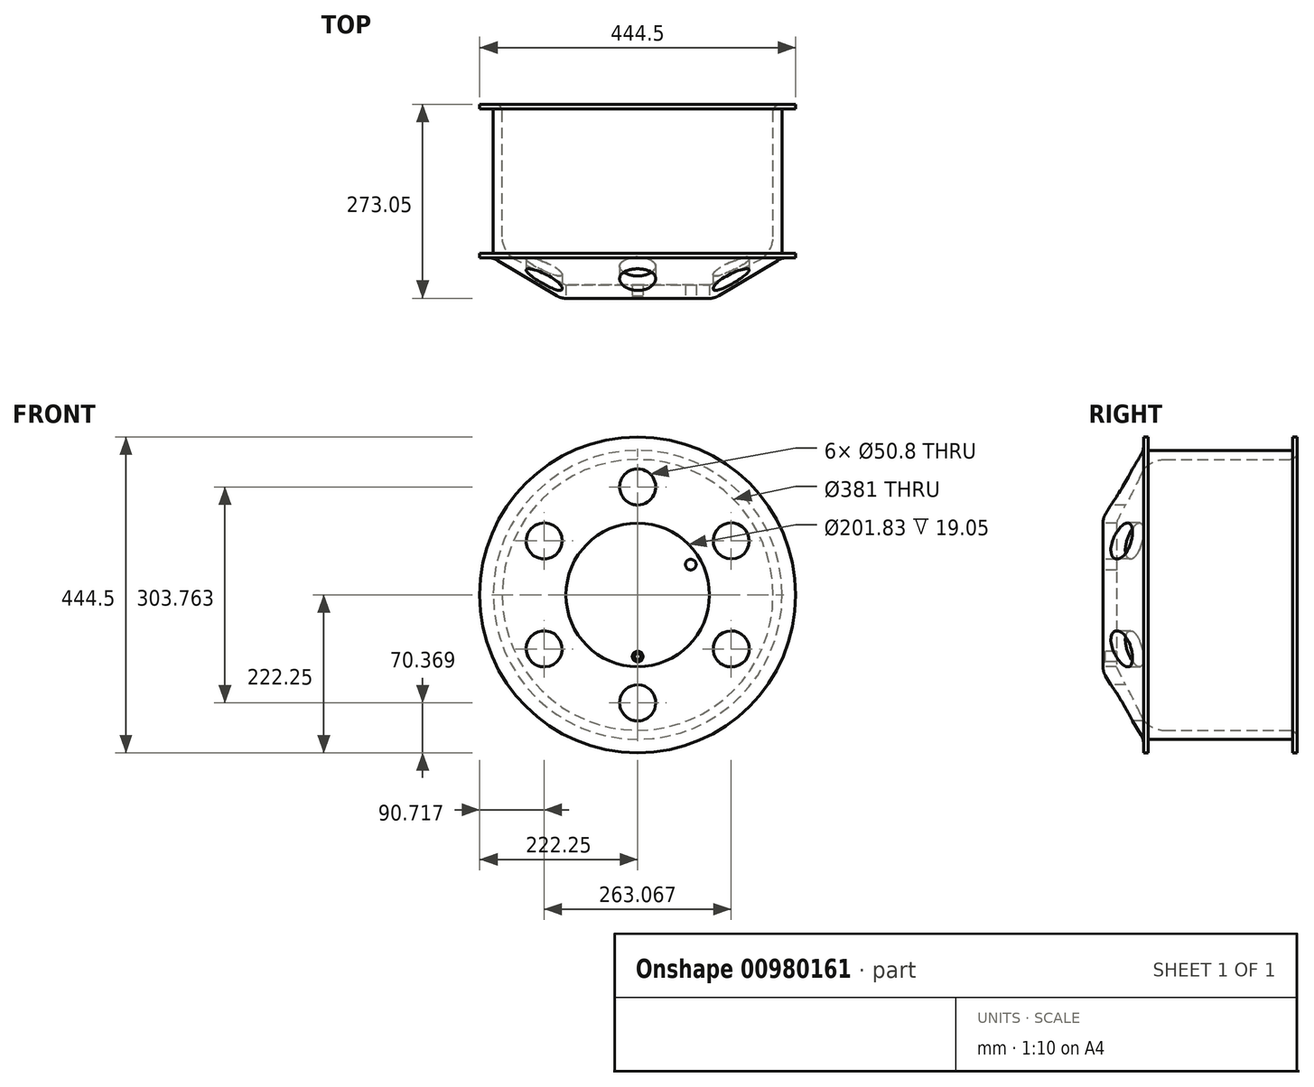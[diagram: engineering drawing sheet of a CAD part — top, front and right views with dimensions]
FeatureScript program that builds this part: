
annotation { "Feature Type Name" : "Feature", "Feature Type Description" : "" }
export const myFeature = defineFeature(function(context is Context, id is Id, definition is map)
    precondition{}
    {
        {
            var Q0;
            Q0=qCreatedBy(makeId("Right.planeOp"),FACE);
            var sketch = newSketch(context, id + "F0", { "sketchPlane" : qUnion([Q0])});
            skLineSegment(sketch, "E0", {"start": v(-78.93, 190.5) * mm, "end": v(96.9, 190.5) * mm});
            skLineSegment(sketch, "E1", {"start": v(107.07, 200.66) * mm, "end": v(107.07, 222.25) * mm});
            skLineSegment(sketch, "E2", {"start": v(107.07, 222.25) * mm, "end": v(100.72, 222.25) * mm});
            skLineSegment(sketch, "E3", {"start": v(100.72, 222.25) * mm, "end": v(100.72, 205.95) * mm});
            skLineSegment(sketch, "E4", {"start": v(97.97, 203.2) * mm, "end": v(-99.73, 203.2) * mm});
            skLineSegment(sketch, "E5", {"start": v(-102.48, 205.95) * mm, "end": v(-102.48, 222.25) * mm});
            skLineSegment(sketch, "E6", {"start": v(-102.48, 222.25) * mm, "end": v(-108.83, 222.25) * mm});
            skLineSegment(sketch, "E7", {"start": v(-108.83, 222.25) * mm, "end": v(-108.83, 210.24) * mm});
            skLineSegment(sketch, "E8", {"start": v(-112.45, 197.17) * mm, "end": v(-162.36, 113.98) * mm});
            skLineSegment(sketch, "E9", {"start": v(-165.98, 100.91) * mm, "end": v(-165.98, 0) * mm});
            skLineSegment(sketch, "E10", {"start": v(-165.98, 0) * mm, "end": v(-146.93, 0) * mm});
            skLineSegment(sketch, "E11", {"start": v(-146.93, 0) * mm, "end": v(-146.93, 101.6) * mm});
            skLineSegment(sketch, "E12", {"start": v(-146.93, 101.6) * mm, "end": v(-113.01, 169.44) * mm});
            skPoint(sketch, "E13.visualSharp", {"position": v(-102.48, 190.5) * mm});
            skArc(sketch, "E13.filletArc", {"start": v(-78.93, 190.5) * mm, "mid": v(-98.96, 184.8) * mm, "end": v(-113.01, 169.44) * mm});
            skPoint(sketch, "E14.visualSharp", {"position": v(-165.98, 107.95) * mm});
            skArc(sketch, "E14.filletArc", {"start": v(-162.36, 113.98) * mm, "mid": v(-165.06, 107.7) * mm, "end": v(-165.98, 100.91) * mm});
            skPoint(sketch, "E15.visualSharp", {"position": v(-108.83, 203.2) * mm});
            skArc(sketch, "E15.filletArc", {"start": v(-112.45, 197.17) * mm, "mid": v(-109.75, 203.46) * mm, "end": v(-108.83, 210.24) * mm});
            skPoint(sketch, "E16.visualSharp", {"position": v(-102.48, 203.2) * mm});
            skArc(sketch, "E16.filletArc", {"start": v(-102.48, 205.95) * mm, "mid": v(-101.68, 204) * mm, "end": v(-99.73, 203.2) * mm});
            skPoint(sketch, "E17.visualSharp", {"position": v(100.72, 203.2) * mm});
            skArc(sketch, "E17.filletArc", {"start": v(97.97, 203.2) * mm, "mid": v(99.92, 204) * mm, "end": v(100.72, 205.95) * mm});
            skPoint(sketch, "E18.visualSharp", {"position": v(107.07, 190.5) * mm});
            skArc(sketch, "E18.filletArc", {"start": v(96.9, 190.5) * mm, "mid": v(104.1, 193.48) * mm, "end": v(107.07, 200.66) * mm});
            skLineSegment(sketch, "E19", {"start": v(0, 0) * mm, "end": v(-85.99, 0) * mm});
            skSolve(sketch);
        }
        {
            var Q0;
            Q0=makeQuery(id+"F0.imprint","IMPRINT",FACE,{"disambiguationData":[TD([[makeQuery(id+"F0.imprint","IMPRINT",EDGE,{"derivedFrom":sQuery(id+"F0.wireOp",EDGE,"E0")}),1.0]])]});
            var Q1;
            Q1=sQuery(id+"F0.wireOp",EDGE,"E19");
            revolve(context, id + "F1", {"surfaceOperationType" : NewSurfaceOperationType.NEW, "entities" : qUnion([Q0]), "axis" : qUnion([Q1]), "revolveType" : RevolveType.FULL});
        }
        {
            var Q0;
            Q0=makeQuery(id+"F1.opRevolve","SWEPT_FACE",FACE,{"disambiguationData":[OSD([sQuery(id+"F0.wireOp",EDGE,"E9")])]});
            var sketch = newSketch(context, id + "F2", { "sketchPlane" : qUnion([Q0])});
            skCircle(sketch, "E20", {"center": v(0, 0) * mm, "radius": 85.72 * mm});
            skCircle(sketch, "E21", {"center": v(0, 85.73) * mm, "radius": 7.5 * mm});
            skCircle(sketch, "E22.1.0", {"center": v(-74.69, 42.6) * mm, "radius": 7.5 * mm});
            skCircle(sketch, "E22.2.0", {"center": v(-74.69, -43.64) * mm, "radius": 7.5 * mm});
            skCircle(sketch, "E22.3.0", {"center": v(0, -86.76) * mm, "radius": 7.5 * mm});
            skCircle(sketch, "E22.4.0", {"center": v(74.69, -43.64) * mm, "radius": 7.5 * mm});
            skCircle(sketch, "E22.5.0", {"center": v(74.69, 42.6) * mm, "radius": 7.5 * mm});
            skPoint(sketch, "E22.center", {"position": v(0, -0.52) * mm});
            skCircle(sketch, "E23", {"center": v(0, 0) * mm, "radius": 67.5 * mm});
            skCircle(sketch, "E24", {"center": v(0, 151.88) * mm, "radius": 25.4 * mm});
            skCircle(sketch, "E25.1.0", {"center": v(-131.53, 75.94) * mm, "radius": 25.4 * mm});
            skCircle(sketch, "E25.2.0", {"center": v(-131.53, -75.94) * mm, "radius": 25.4 * mm});
            skCircle(sketch, "E25.3.0", {"center": v(0, -151.88) * mm, "radius": 25.4 * mm});
            skCircle(sketch, "E25.4.0", {"center": v(131.53, -75.94) * mm, "radius": 25.4 * mm});
            skCircle(sketch, "E25.5.0", {"center": v(131.53, 75.94) * mm, "radius": 25.4 * mm});
            skSolve(sketch);
        }
        {
            var Q0;
            Q0=makeQuery(id+"F2.imprint","IMPRINT",FACE,{"disambiguationData":[TD([[makeQuery(id+"F2.imprint","IMPRINT",EDGE,{"derivedFrom":sQuery(id+"F2.wireOp",EDGE,"E24")}),1.0]])]});
            var Q1;
            Q1=makeQuery(id+"F2.imprint","IMPRINT",FACE,{"disambiguationData":[TD([[makeQuery(id+"F2.imprint","IMPRINT",EDGE,{"derivedFrom":sQuery(id+"F2.wireOp",EDGE,"E25.1.0")}),1.0]])]});
            var Q2;
            Q2=makeQuery(id+"F2.imprint","IMPRINT",FACE,{"disambiguationData":[TD([[makeQuery(id+"F2.imprint","IMPRINT",EDGE,{"derivedFrom":sQuery(id+"F2.wireOp",EDGE,"E25.2.0")}),1.0]])]});
            var Q3;
            Q3=makeQuery(id+"F2.imprint","IMPRINT",FACE,{"disambiguationData":[TD([[makeQuery(id+"F2.imprint","IMPRINT",EDGE,{"derivedFrom":sQuery(id+"F2.wireOp",EDGE,"E25.3.0")}),1.0]])]});
            var Q4;
            Q4=makeQuery(id+"F2.imprint","IMPRINT",FACE,{"disambiguationData":[TD([[makeQuery(id+"F2.imprint","IMPRINT",EDGE,{"derivedFrom":sQuery(id+"F2.wireOp",EDGE,"E25.4.0")}),1.0]])]});
            var Q5;
            Q5=makeQuery(id+"F2.imprint","IMPRINT",FACE,{"disambiguationData":[TD([[makeQuery(id+"F2.imprint","IMPRINT",EDGE,{"derivedFrom":sQuery(id+"F2.wireOp",EDGE,"E25.5.0")}),1.0]])]});
            var Q6;
            {var subQ0=sQuery(id+"F2.wireOp",EDGE,"E22.5.0");var subQ1=sQuery(id+"F2.wireOp",EDGE,"E20");var subQ2=makeQuery(id+"F2.imprint","INTERSECT",VERTEX,{"disambiguationData":[OD(0.0)],"derivedFrom":[subQ1,subQ0]});Q6=makeQuery(id+"F2.imprint","IMPRINT",FACE,{"disambiguationData":[TD([[makeQuery(id+"F2.imprint","IMPRINT",EDGE,{"disambiguationData":[TD([[subQ2,1.0]])],"derivedFrom":subQ1}),1.0]])]});}
            var Q7;
            {var subQ0=sQuery(id+"F2.wireOp",EDGE,"E22.5.0");var subQ1=sQuery(id+"F2.wireOp",EDGE,"E20");var subQ2=makeQuery(id+"F2.imprint","INTERSECT",VERTEX,{"disambiguationData":[OD(0.0)],"derivedFrom":[subQ1,subQ0]});Q7=makeQuery(id+"F2.imprint","IMPRINT",FACE,{"disambiguationData":[TD([[makeQuery(id+"F2.imprint","IMPRINT",EDGE,{"disambiguationData":[TD([[subQ2,1.0]])],"derivedFrom":subQ1}),-1.0]])]});}
            var Q8;
            {var subQ0=sQuery(id+"F2.wireOp",EDGE,"E21");var subQ1=sQuery(id+"F2.wireOp",EDGE,"E20");var subQ2=makeQuery(id+"F2.imprint","INTERSECT",VERTEX,{"disambiguationData":[OD(0.0)],"derivedFrom":[subQ1,subQ0]});Q8=makeQuery(id+"F2.imprint","IMPRINT",FACE,{"disambiguationData":[TD([[makeQuery(id+"F2.imprint","IMPRINT",EDGE,{"disambiguationData":[TD([[subQ2,-1.0]])],"derivedFrom":subQ1}),1.0]])]});}
            var Q9;
            {var subQ0=sQuery(id+"F2.wireOp",EDGE,"E21");var subQ1=sQuery(id+"F2.wireOp",EDGE,"E20");var subQ2=makeQuery(id+"F2.imprint","INTERSECT",VERTEX,{"disambiguationData":[OD(0.0)],"derivedFrom":[subQ1,subQ0]});Q9=makeQuery(id+"F2.imprint","IMPRINT",FACE,{"disambiguationData":[TD([[makeQuery(id+"F2.imprint","IMPRINT",EDGE,{"disambiguationData":[TD([[subQ2,-1.0]])],"derivedFrom":subQ1}),-1.0]])]});}
            var Q10;
            {var subQ0=sQuery(id+"F2.wireOp",EDGE,"E22.1.0");var subQ1=sQuery(id+"F2.wireOp",EDGE,"E20");var subQ2=makeQuery(id+"F2.imprint","INTERSECT",VERTEX,{"disambiguationData":[OD(0.0)],"derivedFrom":[subQ1,subQ0]});Q10=makeQuery(id+"F2.imprint","IMPRINT",FACE,{"disambiguationData":[TD([[makeQuery(id+"F2.imprint","IMPRINT",EDGE,{"disambiguationData":[TD([[subQ2,-1.0]])],"derivedFrom":subQ1}),1.0]])]});}
            var Q11;
            {var subQ0=sQuery(id+"F2.wireOp",EDGE,"E22.1.0");var subQ1=sQuery(id+"F2.wireOp",EDGE,"E20");var subQ2=makeQuery(id+"F2.imprint","INTERSECT",VERTEX,{"disambiguationData":[OD(0.0)],"derivedFrom":[subQ1,subQ0]});Q11=makeQuery(id+"F2.imprint","IMPRINT",FACE,{"disambiguationData":[TD([[makeQuery(id+"F2.imprint","IMPRINT",EDGE,{"disambiguationData":[TD([[subQ2,-1.0]])],"derivedFrom":subQ1}),-1.0]])]});}
            var Q12;
            {var subQ0=sQuery(id+"F2.wireOp",EDGE,"E22.2.0");var subQ1=sQuery(id+"F2.wireOp",EDGE,"E20");var subQ2=makeQuery(id+"F2.imprint","INTERSECT",VERTEX,{"disambiguationData":[OD(0.0)],"derivedFrom":[subQ1,subQ0]});Q12=makeQuery(id+"F2.imprint","IMPRINT",FACE,{"disambiguationData":[TD([[makeQuery(id+"F2.imprint","IMPRINT",EDGE,{"disambiguationData":[TD([[subQ2,-1.0]])],"derivedFrom":subQ1}),1.0]])]});}
            var Q13;
            {var subQ0=sQuery(id+"F2.wireOp",EDGE,"E22.2.0");var subQ1=sQuery(id+"F2.wireOp",EDGE,"E20");var subQ2=makeQuery(id+"F2.imprint","INTERSECT",VERTEX,{"disambiguationData":[OD(0.0)],"derivedFrom":[subQ1,subQ0]});Q13=makeQuery(id+"F2.imprint","IMPRINT",FACE,{"disambiguationData":[TD([[makeQuery(id+"F2.imprint","IMPRINT",EDGE,{"disambiguationData":[TD([[subQ2,-1.0]])],"derivedFrom":subQ1}),-1.0]])]});}
            var Q14;
            {var subQ0=sQuery(id+"F2.wireOp",EDGE,"E22.3.0");var subQ1=sQuery(id+"F2.wireOp",EDGE,"E20");var subQ2=makeQuery(id+"F2.imprint","INTERSECT",VERTEX,{"disambiguationData":[OD(0.0)],"derivedFrom":[subQ1,subQ0]});Q14=makeQuery(id+"F2.imprint","IMPRINT",FACE,{"disambiguationData":[TD([[makeQuery(id+"F2.imprint","IMPRINT",EDGE,{"disambiguationData":[TD([[subQ2,-1.0]])],"derivedFrom":subQ1}),1.0]])]});}
            var Q15;
            {var subQ0=sQuery(id+"F2.wireOp",EDGE,"E22.3.0");var subQ1=sQuery(id+"F2.wireOp",EDGE,"E20");var subQ2=makeQuery(id+"F2.imprint","INTERSECT",VERTEX,{"disambiguationData":[OD(0.0)],"derivedFrom":[subQ1,subQ0]});Q15=makeQuery(id+"F2.imprint","IMPRINT",FACE,{"disambiguationData":[TD([[makeQuery(id+"F2.imprint","IMPRINT",EDGE,{"disambiguationData":[TD([[subQ2,-1.0]])],"derivedFrom":subQ1}),-1.0]])]});}
            var Q16;
            {var subQ0=sQuery(id+"F2.wireOp",EDGE,"E22.4.0");var subQ1=sQuery(id+"F2.wireOp",EDGE,"E20");var subQ2=makeQuery(id+"F2.imprint","INTERSECT",VERTEX,{"disambiguationData":[OD(0.0)],"derivedFrom":[subQ1,subQ0]});Q16=makeQuery(id+"F2.imprint","IMPRINT",FACE,{"disambiguationData":[TD([[makeQuery(id+"F2.imprint","IMPRINT",EDGE,{"disambiguationData":[TD([[subQ2,-1.0]])],"derivedFrom":subQ1}),1.0]])]});}
            var Q17;
            {var subQ0=sQuery(id+"F2.wireOp",EDGE,"E22.4.0");var subQ1=sQuery(id+"F2.wireOp",EDGE,"E20");var subQ2=makeQuery(id+"F2.imprint","INTERSECT",VERTEX,{"disambiguationData":[OD(0.0)],"derivedFrom":[subQ1,subQ0]});Q17=makeQuery(id+"F2.imprint","IMPRINT",FACE,{"disambiguationData":[TD([[makeQuery(id+"F2.imprint","IMPRINT",EDGE,{"disambiguationData":[TD([[subQ2,-1.0]])],"derivedFrom":subQ1}),-1.0]])]});}
            var Q18;
            Q18=makeQuery(id+"F2.imprint","IMPRINT",FACE,{"disambiguationData":[TD([[makeQuery(id+"F2.imprint","IMPRINT",EDGE,{"derivedFrom":sQuery(id+"F2.wireOp",EDGE,"E23")}),1.0]])]});
            extrude(context, id + "F3", {"entities" : qUnion([Q0, Q1, Q2, Q3, Q4, Q5, Q6, Q7, Q8, Q9, Q10, Q11, Q12, Q13, Q14, Q15, Q16, Q17, Q18]), "operationType" : NewBodyOperationType.REMOVE, "endBound" : BoundingType.THROUGH_ALL, "oppositeDirection" : true, "depth" : 25.4 * mm, "offsetDistance" : 25.4 * mm});
        }
        {
            var Q0;
            Q0=makeQuery(id+"F3.boolean.opBoolean","COPY",EDGE,{"derivedFrom":makeQuery(id+"F3.opExtrude","CAP_EDGE",EDGE,{"disambiguationData":[OSD([sQuery(id+"F2.wireOp",EDGE,"E22.1.0")])],"isStart":true})});
            var Q1;
            Q1=makeQuery(id+"F3.boolean.opBoolean","COPY",EDGE,{"derivedFrom":makeQuery(id+"F3.opExtrude","CAP_EDGE",EDGE,{"disambiguationData":[OSD([sQuery(id+"F2.wireOp",EDGE,"E21")])],"isStart":true})});
            var Q2;
            Q2=makeQuery(id+"F3.boolean.opBoolean","COPY",EDGE,{"derivedFrom":makeQuery(id+"F3.opExtrude","CAP_EDGE",EDGE,{"disambiguationData":[OSD([sQuery(id+"F2.wireOp",EDGE,"E22.5.0")])],"isStart":true})});
            var Q3;
            Q3=makeQuery(id+"F3.boolean.opBoolean","COPY",EDGE,{"derivedFrom":makeQuery(id+"F3.opExtrude","CAP_EDGE",EDGE,{"disambiguationData":[OSD([sQuery(id+"F2.wireOp",EDGE,"E22.4.0")])],"isStart":true})});
            var Q4;
            Q4=makeQuery(id+"F3.boolean.opBoolean","COPY",EDGE,{"derivedFrom":makeQuery(id+"F3.opExtrude","CAP_EDGE",EDGE,{"disambiguationData":[OSD([sQuery(id+"F2.wireOp",EDGE,"E22.3.0")])],"isStart":true})});
            var Q5;
            Q5=makeQuery(id+"F3.boolean.opBoolean","COPY",EDGE,{"derivedFrom":makeQuery(id+"F3.opExtrude","CAP_EDGE",EDGE,{"disambiguationData":[OSD([sQuery(id+"F2.wireOp",EDGE,"E22.2.0")])],"isStart":true})});
            chamfer(context, id + "F4", {"entities" : qUnion([Q0, Q1, Q2, Q3, Q4, Q5]), "width" : 3.17 * mm, "tangentPropagation" : true});
        }
    });
